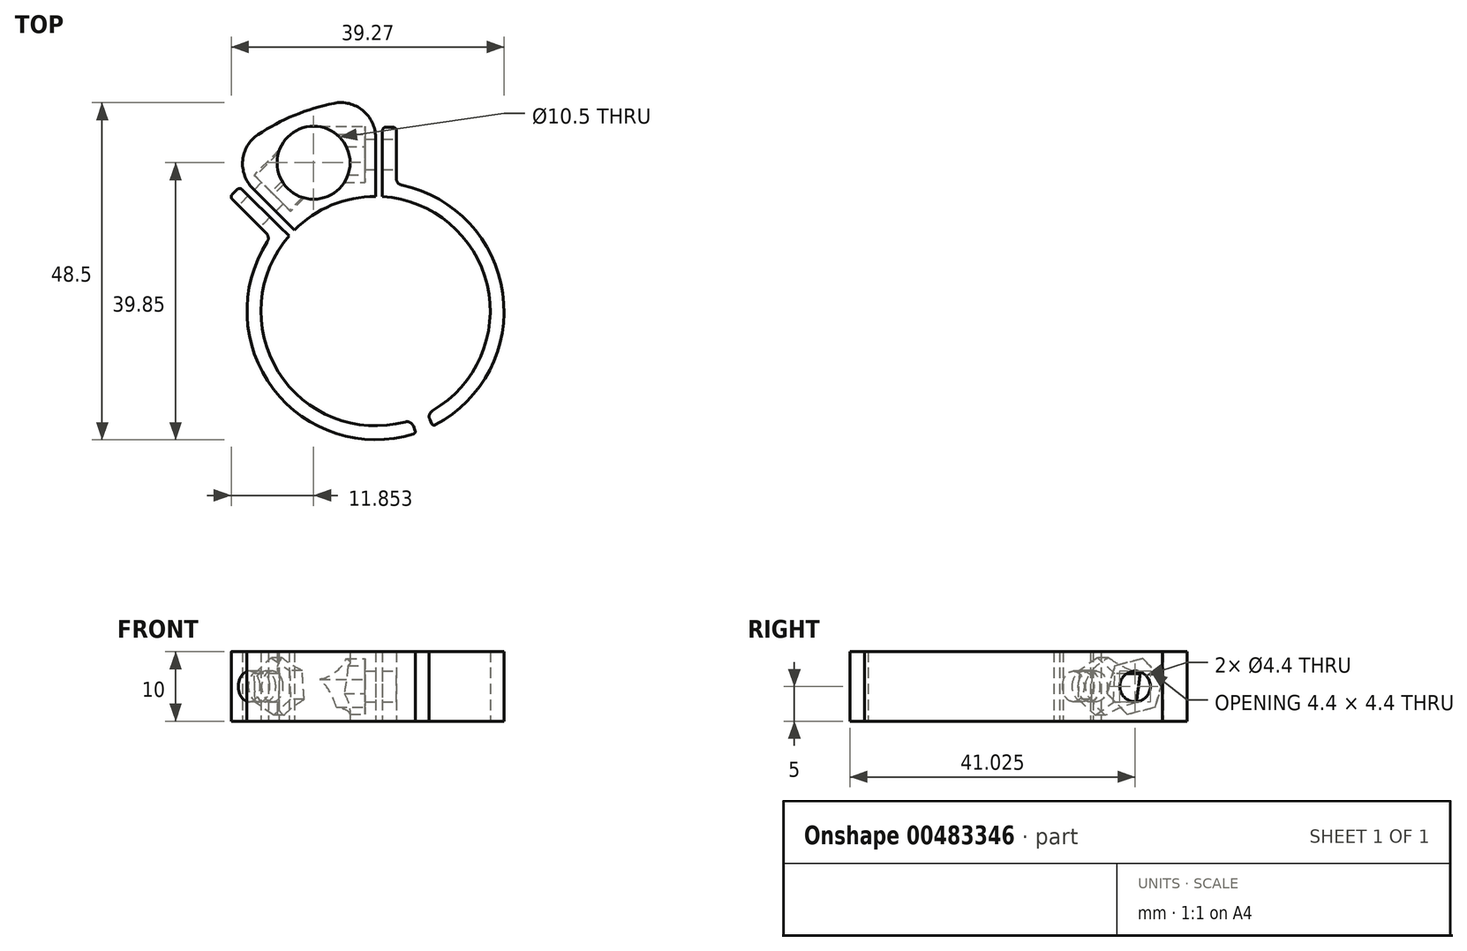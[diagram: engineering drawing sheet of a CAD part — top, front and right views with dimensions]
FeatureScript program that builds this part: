
annotation { "Feature Type Name" : "Feature", "Feature Type Description" : "" }
export const myFeature = defineFeature(function(context is Context, id is Id, definition is map)
    precondition{}
    {
        {
            var Q0;
            Q0=qCreatedBy(makeId("Top.planeOp"),FACE);
            var sketch = newSketch(context, id + "F0", { "sketchPlane" : qUnion([Q0])});
            skLineSegment(sketch, "E0", {"start": v(0, 18.5) * mm, "end": v(0, 18.5) * mm});
            skArc(sketch, "E1", {"start": v(-16.92, 25.37) * mm, "mid": v(-11.67, 28.17) * mm, "end": v(-5.98, 29.9) * mm});
            skLineSegment(sketch, "E2", {"start": v(0, 18.5) * mm, "end": v(0, 25) * mm});
            skLineSegment(sketch, "E3", {"start": v(0, 0) * mm, "end": v(-17.68, 17.68) * mm});
            skLineSegment(sketch, "E4", {"start": v(0, 18.5) * mm, "end": v(0, 24.5) * mm});
            skCircle(sketch, "E5", {"center": v(-8.92, 21.35) * mm, "radius": 5.25 * mm});
            skLineSegment(sketch, "E6", {"start": v(1, 18.47) * mm, "end": v(1, 18.47) * mm});
            skLineSegment(sketch, "E7", {"start": v(1, 18.47) * mm, "end": v(1, 25.97) * mm});
            skLineSegment(sketch, "E8", {"start": v(0, 16.5) * mm, "end": v(0, 18.5) * mm});
            skLineSegment(sketch, "E9", {"start": v(1, 18.47) * mm, "end": v(1, 16.47) * mm});
            skArc(sketch, "E10", {"start": v(0, 16.5) * mm, "mid": v(-6.31, 15.24) * mm, "end": v(-11.67, 11.67) * mm});
            skLineSegment(sketch, "E11", {"start": v(1.5, 26.47) * mm, "end": v(2.5, 26.47) * mm});
            skLineSegment(sketch, "E12", {"start": v(3, 25.97) * mm, "end": v(3, 19.08) * mm});
            skArc(sketch, "E13", {"start": v(3.8, 18.1) * mm, "mid": v(18.32, 2.55) * mm, "end": v(8.6, -16.38) * mm});
            skLineSegment(sketch, "E14", {"start": v(-13.9, 12.2) * mm, "end": v(-19.2, 17.5) * mm});
            skLineSegment(sketch, "E15", {"start": v(-19.91, 17.5) * mm, "end": v(-20.62, 16.8) * mm});
            skLineSegment(sketch, "E16", {"start": v(-20.62, 16.09) * mm, "end": v(-15.73, 11.2) * mm});
            skLineSegment(sketch, "E17", {"start": v(-15.15, 10.61) * mm, "end": v(-15.15, 10.61) * mm});
            skLineSegment(sketch, "E18", {"start": v(-13.9, 12.2) * mm, "end": v(-12.42, 10.86) * mm});
            skArc(sketch, "E19", {"start": v(-12.42, 10.86) * mm, "mid": v(-14, -8.72) * mm, "end": v(4.26, -15.94) * mm});
            skPoint(sketch, "E20.visualSharp", {"position": v(-21.56, 21.56) * mm});
            skArc(sketch, "E20.filletArc", {"start": v(-16.92, 25.37) * mm, "mid": v(-19.12, 21.7) * mm, "end": v(-17.68, 17.68) * mm});
            skPoint(sketch, "E21.visualSharp", {"position": v(0, 30.5) * mm});
            skArc(sketch, "E21.filletArc", {"start": v(0, 25) * mm, "mid": v(-1.83, 28.87) * mm, "end": v(-5.98, 29.9) * mm});
            skPoint(sketch, "E22.visualSharp", {"position": v(1, 26.47) * mm});
            skArc(sketch, "E22.filletArc", {"start": v(1.5, 26.47) * mm, "mid": v(1.15, 26.32) * mm, "end": v(1, 25.97) * mm});
            skPoint(sketch, "E23.visualSharp", {"position": v(3, 26.47) * mm});
            skArc(sketch, "E23.filletArc", {"start": v(3, 25.97) * mm, "mid": v(2.85, 26.32) * mm, "end": v(2.5, 26.47) * mm});
            skPoint(sketch, "E24.visualSharp", {"position": v(-20.97, 16.44) * mm});
            skArc(sketch, "E24.filletArc", {"start": v(-20.62, 16.8) * mm, "mid": v(-20.77, 16.44) * mm, "end": v(-20.62, 16.09) * mm});
            skPoint(sketch, "E25.visualSharp", {"position": v(-19.56, 17.86) * mm});
            skArc(sketch, "E25.filletArc", {"start": v(-19.2, 17.5) * mm, "mid": v(-19.56, 17.65) * mm, "end": v(-19.91, 17.5) * mm});
            skPoint(sketch, "E26.visualSharp", {"position": v(3, 18.25) * mm});
            skArc(sketch, "E26.filletArc", {"start": v(3, 19.08) * mm, "mid": v(3.22, 18.45) * mm, "end": v(3.8, 18.1) * mm});
            skPoint(sketch, "E27.visualSharp", {"position": v(-15.15, 10.61) * mm});
            skArc(sketch, "E27.filletArc", {"start": v(-15.6, 9.95) * mm, "mid": v(-15.44, 10.6) * mm, "end": v(-15.73, 11.2) * mm});
            skLineSegment(sketch, "E28", {"start": v(5.12, -15.69) * mm, "end": v(5.12, -15.69) * mm});
            skLineSegment(sketch, "E29", {"start": v(8.26, -16.55) * mm, "end": v(8.26, -16.55) * mm});
            skLineSegment(sketch, "E30", {"start": v(5.83, -17.55) * mm, "end": v(5.83, -17.55) * mm});
            skArc(sketch, "E31", {"start": v(8.22, -14.3) * mm, "mid": v(16.06, 3.77) * mm, "end": v(1, 16.47) * mm});
            skLineSegment(sketch, "E32", {"start": v(8.1, -16.2) * mm, "end": v(7.81, -15.6) * mm});
            skLineSegment(sketch, "E33", {"start": v(5.45, -16.56) * mm, "end": v(5.7, -17.2) * mm});
            skArc(sketch, "E34", {"start": v(5.46, -17.67) * mm, "mid": v(-14.71, -11.21) * mm, "end": v(-15.6, 9.95) * mm});
            skPoint(sketch, "E35.visualSharp", {"position": v(5.12, -15.69) * mm});
            skArc(sketch, "E35.filletArc", {"start": v(5.45, -16.56) * mm, "mid": v(4.97, -16.02) * mm, "end": v(4.26, -15.94) * mm});
            skPoint(sketch, "E36.visualSharp", {"position": v(5.83, -17.55) * mm});
            skArc(sketch, "E36.filletArc", {"start": v(5.46, -17.67) * mm, "mid": v(5.68, -17.48) * mm, "end": v(5.7, -17.2) * mm});
            skPoint(sketch, "E37.visualSharp", {"position": v(7.42, -14.74) * mm});
            skArc(sketch, "E37.filletArc", {"start": v(8.22, -14.3) * mm, "mid": v(7.77, -14.87) * mm, "end": v(7.81, -15.6) * mm});
            skPoint(sketch, "E38.visualSharp", {"position": v(8.26, -16.55) * mm});
            skArc(sketch, "E38.filletArc", {"start": v(8.1, -16.2) * mm, "mid": v(8.31, -16.4) * mm, "end": v(8.6, -16.38) * mm});
            skSolve(sketch);
        }
        {
            var Q0;
            Q0=qSketchRegion(id+"F0",true);
            extrude(context, id + "F1", {"entities" : qUnion([Q0]), "depth" : 10 * mm});
        }
        {
            var Q0;
            Q0=makeQuery(id+"F1.opExtrude","SWEPT_FACE",FACE,{"disambiguationData":[OSD([sQuery(id+"F0.wireOp",EDGE,"E12")])]});
            var sketch = newSketch(context, id + "F2", { "sketchPlane" : qUnion([Q0])});
            skCircle(sketch, "E39", {"center": v(22.52, 5) * mm, "radius": 2.2 * mm});
            skPoint(sketch, "E39.centerSnap0", {"position": v(22.52, 0) * mm});
            skPoint(sketch, "E39.centerSnap1", {"position": v(19.08, 5) * mm});
            skSolve(sketch);
        }
        {
            var Q0;
            Q0=qSketchRegion(id+"F2",true);
            extrude(context, id + "F3", {"entities" : qUnion([Q0]), "operationType" : NewBodyOperationType.REMOVE, "oppositeDirection" : true, "depth" : 8 * mm});
        }
        {
            var Q0;
            Q0=makeQuery(id+"F1.opExtrude","SWEPT_FACE",FACE,{"disambiguationData":[OSD([sQuery(id+"F0.wireOp",EDGE,"E16")])]});
            var sketch = newSketch(context, id + "F4", { "sketchPlane" : qUnion([Q0])});
            skCircle(sketch, "E40", {"center": v(-22.5, 5) * mm, "radius": 2.2 * mm});
            skPoint(sketch, "E40.centerSnap0", {"position": v(-22.5, 10) * mm});
            skPoint(sketch, "E40.centerSnap1", {"position": v(-19.04, 5) * mm});
            skSolve(sketch);
        }
        {
            var Q0;
            Q0=makeQuery(id+"F4.imprint","IMPRINT",FACE,{"disambiguationData":[TD([[makeQuery(id+"F4.imprint","IMPRINT",EDGE,{"derivedFrom":sQuery(id+"F4.wireOp",EDGE,"E40")}),1.0]])]});
            extrude(context, id + "F5", {"entities" : qUnion([Q0]), "operationType" : NewBodyOperationType.REMOVE, "oppositeDirection" : true, "depth" : 10 * mm});
        }
        {
            var Q0;
            Q0=makeQuery(id+"F1.opExtrude","SWEPT_FACE",FACE,{"disambiguationData":[OSD([sQuery(id+"F0.wireOp",EDGE,"E3")])]});
            var sketch = newSketch(context, id + "F6", { "sketchPlane" : qUnion([Q0])});
            skCircle(sketch, "E41.cCircle", {"center": v(-22.5, 5) * mm, "radius": 3.6 * mm, "construction": true});
            skLineSegment(sketch, "E41.0", {"start": v(-22.75, 9.15) * mm, "end": v(-19.03, 7.3) * mm});
            skLineSegment(sketch, "E41.1", {"start": v(-19.03, 7.3) * mm, "end": v(-18.78, 3.14) * mm});
            skLineSegment(sketch, "E41.2", {"start": v(-18.78, 3.14) * mm, "end": v(-22.24, 0.85) * mm});
            skLineSegment(sketch, "E41.3", {"start": v(-22.24, 0.85) * mm, "end": v(-25.96, 2.7) * mm});
            skLineSegment(sketch, "E41.4", {"start": v(-25.96, 2.7) * mm, "end": v(-26.22, 6.86) * mm});
            skLineSegment(sketch, "E41.5", {"start": v(-26.22, 6.86) * mm, "end": v(-22.75, 9.15) * mm});
            skPoint(sketch, "E41.0.midPoint", {"position": v(-20.89, 8.22) * mm});
            skSolve(sketch);
        }
        {
            var Q0;
            Q0=makeQuery(id+"F6.imprint","IMPRINT",FACE,{"disambiguationData":[TD([[makeQuery(id+"F6.imprint","IMPRINT",EDGE,{"derivedFrom":makeQuery(id+"F5.boolean.opBoolean","INTERSECT",EDGE,{"derivedFrom":[makeQuery(id+"F1.opExtrude","SWEPT_FACE",FACE,{"disambiguationData":[OSD([sQuery(id+"F0.wireOp",EDGE,"E3")])]}),makeQuery(id+"F5.opExtrude","SWEPT_FACE",FACE,{"disambiguationData":[OSD([sQuery(id+"F4.wireOp",EDGE,"E40")])]})]})}),1.0]])]});
            var Q1;
            {var subQ0=sQuery(id+"F6.wireOp",EDGE,"E41.4");Q1=makeQuery(id+"F6.imprint","IMPRINT",FACE,{"disambiguationData":[TD([[makeQuery(id+"F6.imprint","IMPRINT",EDGE,{"derivedFrom":subQ0}),-1.0]])]});}
            var Q2;
            {var subQ7=sQuery(id+"F6.wireOp",EDGE,"E41.0");Q2=makeQuery(id+"F6.imprint","IMPRINT",FACE,{"disambiguationData":[TD([[makeQuery(id+"F6.imprint","IMPRINT",EDGE,{"derivedFrom":subQ7}),-1.0]])]});}
            extrude(context, id + "F7", {"entities" : qUnion([Q0, Q1, Q2]), "operationType" : NewBodyOperationType.REMOVE, "oppositeDirection" : true, "depth" : 8 * mm, "hasSecondDirection" : true, "secondDirectionOppositeDirection" : true, "secondDirectionDepth" : 1.5 * mm});
        }
        {
            var Q0;
            Q0=makeQuery(id+"F1.opExtrude","SWEPT_FACE",FACE,{"disambiguationData":[OSD([sQuery(id+"F0.wireOp",EDGE,"E2"),sQuery(id+"F0.wireOp",EDGE,"E4"),sQuery(id+"F0.wireOp",EDGE,"E8")])]});
            var sketch = newSketch(context, id + "F8", { "sketchPlane" : qUnion([Q0])});
            skCircle(sketch, "E42.cCircle", {"center": v(22.52, 5) * mm, "radius": 3.6 * mm, "construction": true});
            skLineSegment(sketch, "E42.0", {"start": v(19.62, 7.97) * mm, "end": v(23.64, 9) * mm});
            skLineSegment(sketch, "E42.1", {"start": v(23.64, 9) * mm, "end": v(26.55, 6.03) * mm});
            skLineSegment(sketch, "E42.2", {"start": v(26.55, 6.03) * mm, "end": v(25.43, 2.03) * mm});
            skLineSegment(sketch, "E42.3", {"start": v(25.43, 2.03) * mm, "end": v(21.4, 1) * mm});
            skLineSegment(sketch, "E42.4", {"start": v(21.4, 1) * mm, "end": v(18.5, 3.97) * mm});
            skLineSegment(sketch, "E42.5", {"start": v(18.5, 3.97) * mm, "end": v(19.62, 7.97) * mm});
            skPoint(sketch, "E42.0.midPoint", {"position": v(21.63, 8.49) * mm});
            skSolve(sketch);
        }
        {
            var Q0;
            Q0=qSketchRegion(id+"F8",true);
            extrude(context, id + "F9", {"entities" : qUnion([Q0]), "operationType" : NewBodyOperationType.REMOVE, "oppositeDirection" : true, "depth" : 8 * mm, "hasSecondDirection" : true, "secondDirectionOppositeDirection" : true, "secondDirectionDepth" : 1.5 * mm});
        }
    });
